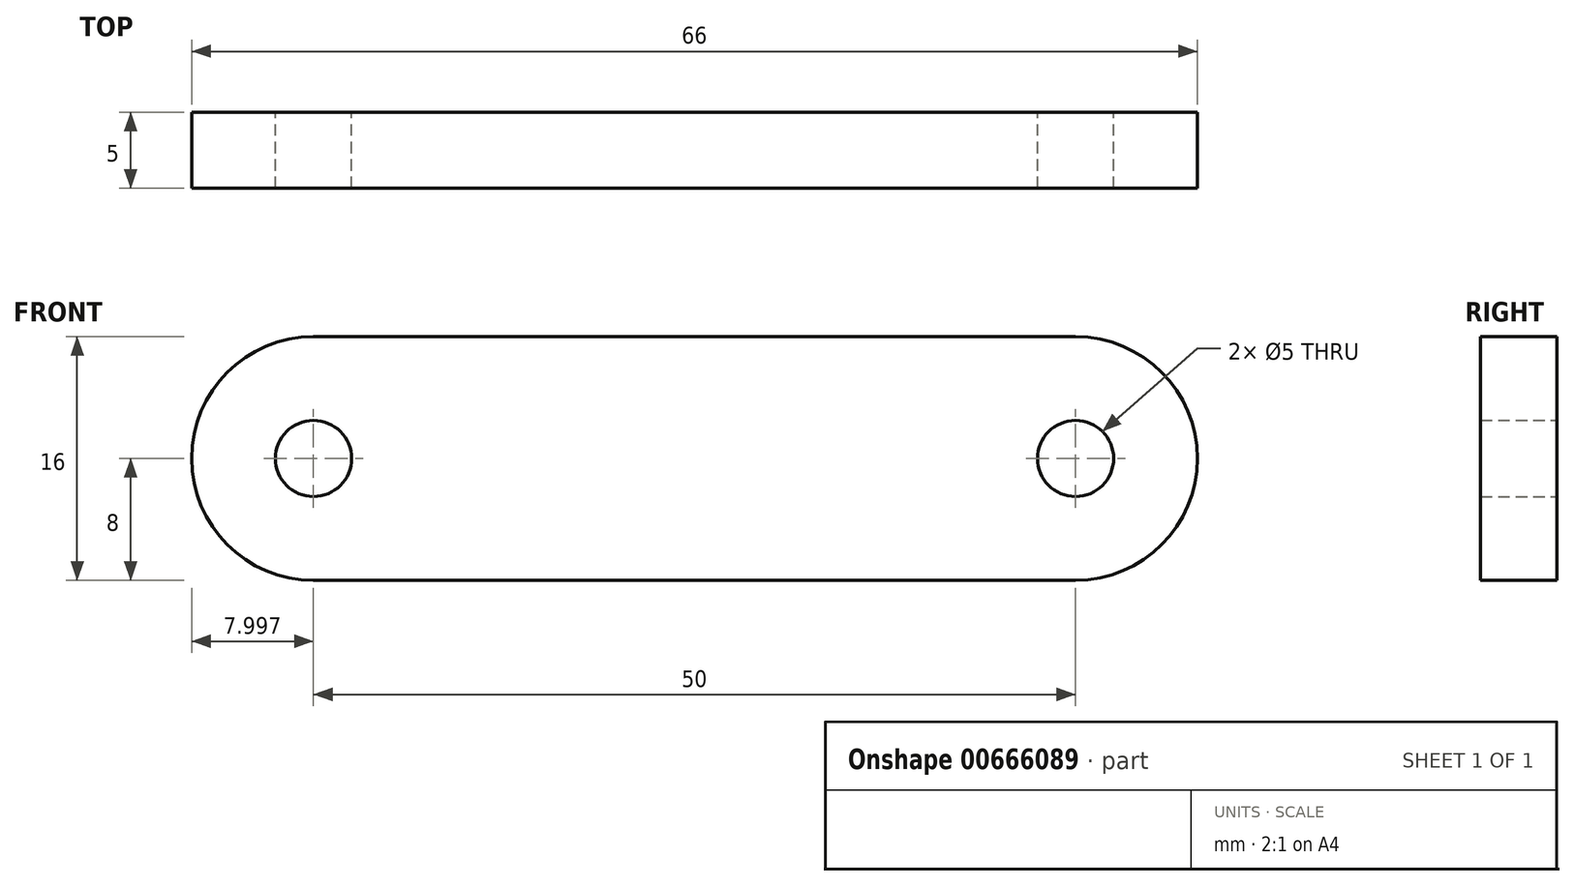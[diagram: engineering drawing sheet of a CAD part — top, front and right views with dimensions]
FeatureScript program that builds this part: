
annotation { "Feature Type Name" : "Feature", "Feature Type Description" : "" }
export const myFeature = defineFeature(function(context is Context, id is Id, definition is map)
    precondition{}
    {
        {
            var Q0;
            Q0=qCreatedBy(makeId("Front.planeOp"),FACE);
            var sketch = newSketch(context, id + "F0", { "sketchPlane" : qUnion([Q0])});
            skLineSegment(sketch, "E0.bottom", {"start": v(-23.08, 8) * mm, "end": v(26.92, 8) * mm});
            skLineSegment(sketch, "E0.top", {"start": v(-23.08, -8) * mm, "end": v(26.92, -8) * mm});
            skArc(sketch, "E1", {"start": v(-23.08, 8) * mm, "mid": v(-31.08, 0) * mm, "end": v(-23.08, -8) * mm});
            skArc(sketch, "E2", {"start": v(26.92, -8) * mm, "mid": v(34.92, 0) * mm, "end": v(26.92, 8) * mm});
            skCircle(sketch, "E3", {"center": v(-23.08, 0) * mm, "radius": 2.5 * mm});
            skCircle(sketch, "E4", {"center": v(26.92, 0) * mm, "radius": 2.5 * mm});
            skSolve(sketch);
        }
        {
            var Q0;
            Q0=makeQuery(id+"F0.imprint","IMPRINT",FACE,{"disambiguationData":[TD([[makeQuery(id+"F0.imprint","IMPRINT",EDGE,{"derivedFrom":sQuery(id+"F0.wireOp",EDGE,"E0.bottom")}),-1.0]])]});
            extrude(context, id + "F1", {"entities" : qUnion([Q0]), "depth" : 5 * mm, "offsetDistance" : 25 * mm});
        }
    });
